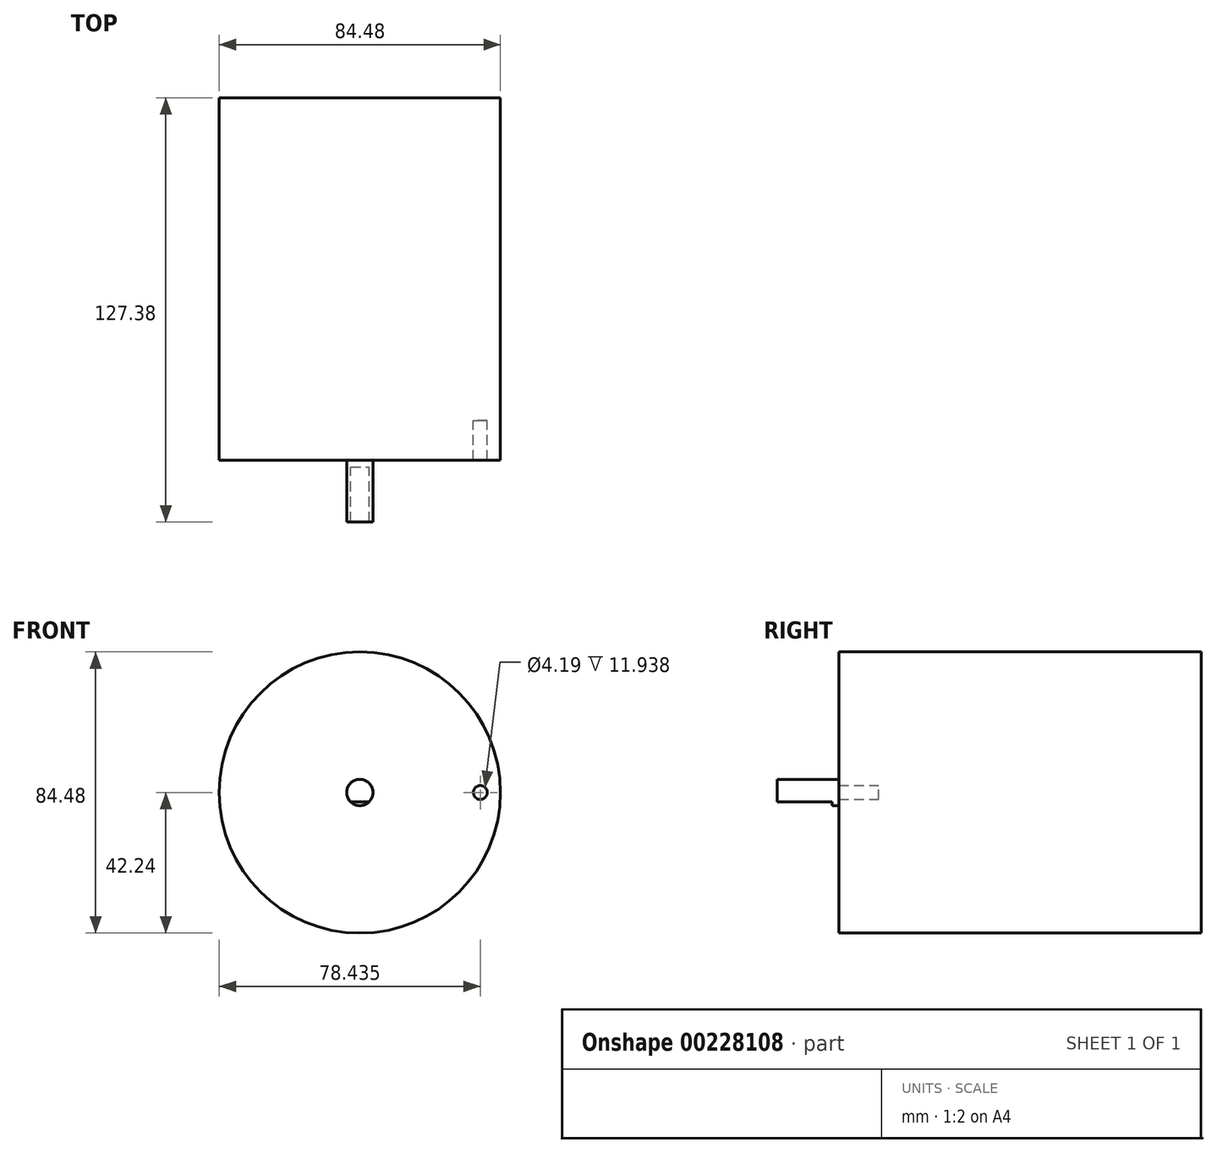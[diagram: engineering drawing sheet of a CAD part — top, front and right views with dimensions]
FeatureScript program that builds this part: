
annotation { "Feature Type Name" : "Feature", "Feature Type Description" : "" }
export const myFeature = defineFeature(function(context is Context, id is Id, definition is map)
    precondition{}
    {
        {
            var Q0;
            Q0=qCreatedBy(makeId("Front.planeOp"),FACE);
            var sketch = newSketch(context, id + "F0", { "sketchPlane" : qUnion([Q0])});
            skCircle(sketch, "E0", {"center": v(0, 0) * mm, "radius": 42.24 * mm});
            skSolve(sketch);
        }
        {
            var Q0;
            Q0=makeQuery(id+"F0.imprint","IMPRINT",FACE,{"disambiguationData":[TD([[makeQuery(id+"F0.imprint","IMPRINT",EDGE,{"derivedFrom":sQuery(id+"F0.wireOp",EDGE,"E0")}),1.0]])]});
            extrude(context, id + "F1", {"entities" : qUnion([Q0]), "depth" : 96.9 * mm});
        }
        {
            var Q0;
            Q0=makeQuery(id+"F1.opExtrude","CAP_FACE",FACE,{"disambiguationData":[OSD([sQuery(id+"F0.wireOp",EDGE,"E0")])],"isStart":false});
            var sketch = newSketch(context, id + "F2", { "sketchPlane" : qUnion([Q0])});
            skCircle(sketch, "E1", {"center": v(0, 0) * mm, "radius": 3.95 * mm});
            skSolve(sketch);
        }
        {
            var Q0;
            Q0=makeQuery(id+"F2.imprint","IMPRINT",FACE,{"disambiguationData":[TD([[makeQuery(id+"F2.imprint","IMPRINT",EDGE,{"derivedFrom":sQuery(id+"F2.wireOp",EDGE,"E1")}),1.0]])]});
            extrude(context, id + "F3", {"entities" : qUnion([Q0]), "operationType" : NewBodyOperationType.ADD, "depth" : 30.48 * mm});
        }
        {
            var Q0;
            Q0=makeQuery(id+"F1.opExtrude","CAP_FACE",FACE,{"disambiguationData":[OSD([sQuery(id+"F0.wireOp",EDGE,"E0")])],"isStart":false});
            var sketch = newSketch(context, id + "F4", { "sketchPlane" : qUnion([Q0])});
            skLineSegment(sketch, "E2", {"start": v(-42.24, 0) * mm, "end": v(42.24, 0) * mm, "construction": true});
            skCircle(sketch, "E3", {"center": v(-36.2, 0) * mm, "radius": 2.1 * mm});
            skLineSegment(sketch, "E4", {"start": v(0, 42.24) * mm, "end": v(0, -42.24) * mm, "construction": true});
            skCircle(sketch, "E5.MirrorC", {"center": v(36.2, 0) * mm, "radius": 2.1 * mm});
            skSolve(sketch);
        }
        {
            var Q0;
            Q0=makeQuery(id+"F4.imprint","IMPRINT",FACE,{"disambiguationData":[TD([[makeQuery(id+"F4.imprint","IMPRINT",EDGE,{"derivedFrom":sQuery(id+"F4.wireOp",EDGE,"E3")}),1.0]])]});
            var Q1;
            Q1=makeQuery(id+"F4.imprint","IMPRINT",FACE,{"disambiguationData":[TD([[makeQuery(id+"F4.imprint","IMPRINT",EDGE,{"derivedFrom":sQuery(id+"F4.wireOp",EDGE,"E5.MirrorC")}),-1.0]])]});
            extrude(context, id + "F5", {"entities" : qUnion([Q0, Q1]), "operationType" : NewBodyOperationType.ADD, "depth" : 11.94 * mm});
        }
        {
            var Q0;
            Q0=makeQuery(id+"F3.opExtrude","CAP_FACE",FACE,{"disambiguationData":[OSD([sQuery(id+"F2.wireOp",EDGE,"E1")])],"isStart":false});
            var sketch = newSketch(context, id + "F6", { "sketchPlane" : qUnion([Q0])});
            skLineSegment(sketch, "E6.bottom", {"start": v(-4.58, -2.8) * mm, "end": v(4.58, -2.8) * mm});
            skLineSegment(sketch, "E6.top", {"start": v(-4.58, -6.13) * mm, "end": v(4.58, -6.13) * mm});
            skLineSegment(sketch, "E6.left", {"start": v(-4.58, -2.8) * mm, "end": v(-4.58, -6.13) * mm});
            skLineSegment(sketch, "E6.right", {"start": v(4.58, -2.8) * mm, "end": v(4.58, -6.13) * mm});
            skLineSegment(sketch, "E7.bottom", {"start": v(0, 3.95) * mm, "end": v(0, 3.95) * mm});
            skLineSegment(sketch, "E7.top", {"start": v(0, -3.95) * mm, "end": v(0, -3.95) * mm});
            skLineSegment(sketch, "E7.left", {"start": v(0, 3.95) * mm, "end": v(0, -3.95) * mm, "construction": true});
            skLineSegment(sketch, "E7.right", {"start": v(0, 3.95) * mm, "end": v(0, -3.95) * mm, "construction": true});
            skPoint(sketch, "E8", {"position": v(0, -2.8) * mm});
            skSolve(sketch);
        }
        {
            var Q0;
            Q0=makeQuery(id+"F6.imprint","IMPRINT",FACE,{"disambiguationData":[TD([[makeQuery(id+"F6.imprint","IMPRINT",EDGE,{"derivedFrom":sQuery(id+"F6.wireOp",EDGE,"E6.top")}),1.0]])]});
            var Q1;
            {var subQ0=sQuery(id+"F6.wireOp",EDGE,"E6.bottom");var subQ1=makeQuery(id+"F3.opExtrude","CAP_EDGE",EDGE,{"disambiguationData":[OSD([sQuery(id+"F2.wireOp",EDGE,"E1")])],"isStart":false});var subQ2=makeQuery(id+"F6.imprint","INTERSECT",VERTEX,{"disambiguationData":[OD(0.0)],"derivedFrom":[subQ1,subQ0]});Q1=makeQuery(id+"F6.imprint","IMPRINT",FACE,{"disambiguationData":[TD([[makeQuery(id+"F6.imprint","IMPRINT",EDGE,{"disambiguationData":[TD([[subQ2,-1.0]])],"derivedFrom":subQ0}),-1.0]])]});}
            extrude(context, id + "F7", {"entities" : qUnion([Q0, Q1]), "operationType" : NewBodyOperationType.REMOVE, "oppositeDirection" : true, "depth" : 16.5 * mm});
        }
    });
